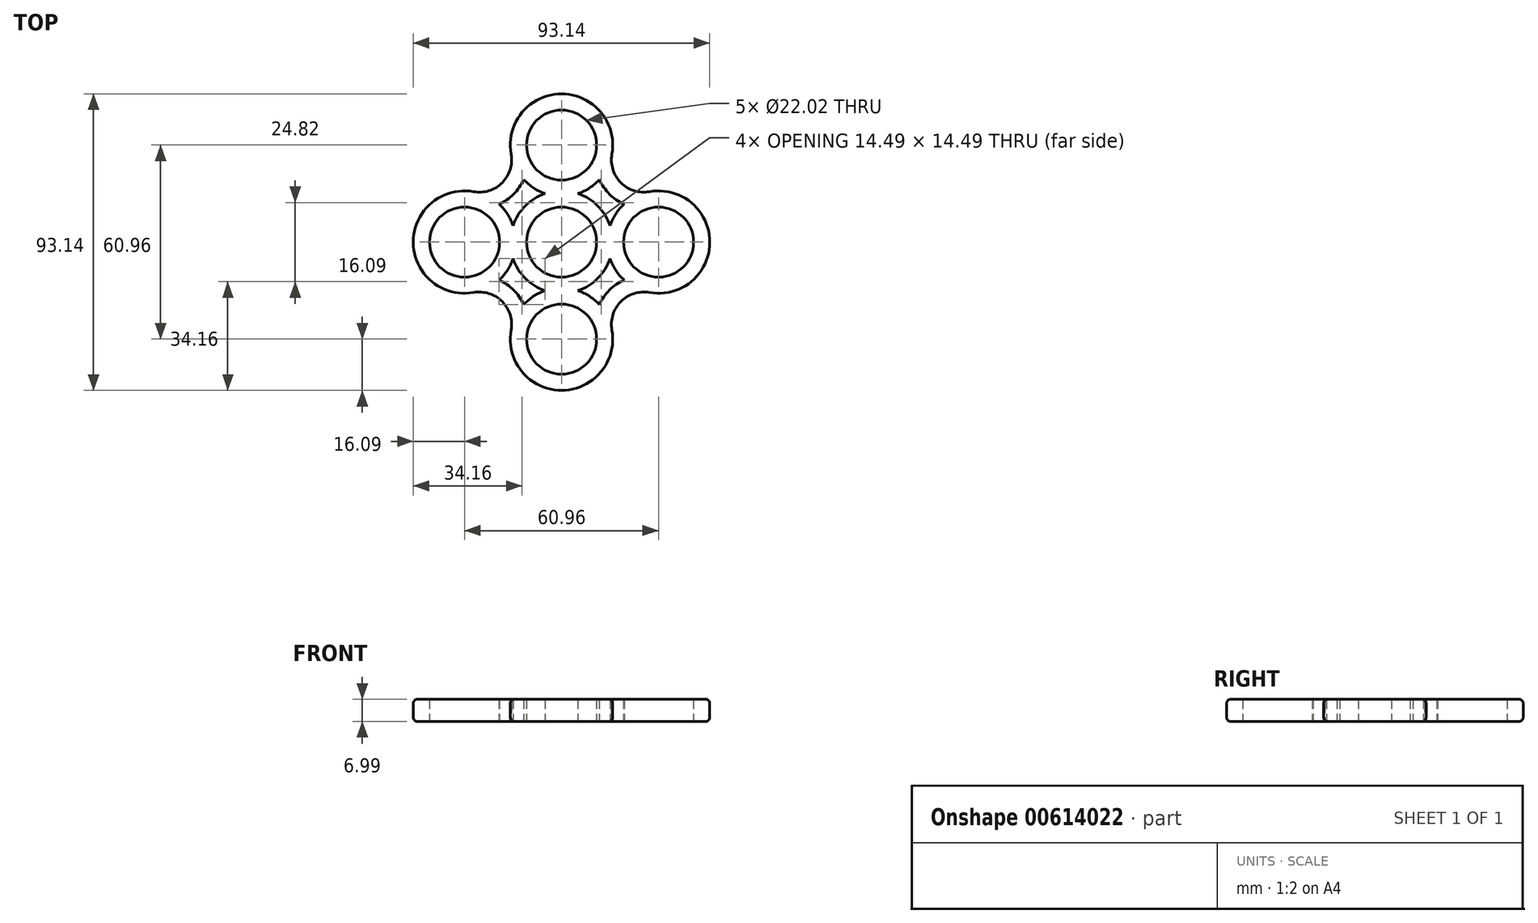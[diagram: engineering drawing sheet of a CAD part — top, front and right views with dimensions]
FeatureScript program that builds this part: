
annotation { "Feature Type Name" : "Feature", "Feature Type Description" : "" }
export const myFeature = defineFeature(function(context is Context, id is Id, definition is map)
    precondition{}
    {
        {
            var Q0;
            Q0=qCreatedBy(makeId("Top.planeOp"),FACE);
            var sketch = newSketch(context, id + "F0", { "sketchPlane" : qUnion([Q0])});
            skCircle(sketch, "E0", {"center": v(0, 0) * mm, "radius": 11.01 * mm});
            skLineSegment(sketch, "E1", {"start": v(0, 0) * mm, "end": v(0, 30.48) * mm});
            skLineSegment(sketch, "E2", {"start": v(0, 0) * mm, "end": v(-30.48, 0) * mm});
            skLineSegment(sketch, "E3", {"start": v(0, 0) * mm, "end": v(30.48, 0) * mm});
            skLineSegment(sketch, "E4", {"start": v(0, 0) * mm, "end": v(0, -30.48) * mm});
            skCircle(sketch, "E5", {"center": v(-30.48, 0) * mm, "radius": 11.01 * mm});
            skCircle(sketch, "E6", {"center": v(0, 30.48) * mm, "radius": 11.01 * mm});
            skCircle(sketch, "E7", {"center": v(30.48, 0) * mm, "radius": 11.01 * mm});
            skCircle(sketch, "E8", {"center": v(-30.48, 0) * mm, "radius": 16.1 * mm});
            skCircle(sketch, "E9", {"center": v(0, 0) * mm, "radius": 17.78 * mm});
            skCircle(sketch, "E10", {"center": v(0, -30.48) * mm, "radius": 16.1 * mm});
            skCircle(sketch, "E11", {"center": v(30.48, 0) * mm, "radius": 16.1 * mm});
            skCircle(sketch, "E12", {"center": v(0, 30.48) * mm, "radius": 16.1 * mm});
            skCircle(sketch, "E13", {"center": v(0, -30.48) * mm, "radius": 11.01 * mm});
            skArc(sketch, "E14", {"start": v(27.63, -15.84) * mm, "mid": v(18.65, -18.65) * mm, "end": v(15.84, -27.63) * mm});
            skArc(sketch, "E15", {"start": v(-15.84, -27.63) * mm, "mid": v(-18.65, -18.65) * mm, "end": v(-27.63, -15.84) * mm});
            skArc(sketch, "E16", {"start": v(15.84, 27.63) * mm, "mid": v(18.65, 18.65) * mm, "end": v(27.63, 15.84) * mm});
            skArc(sketch, "E17", {"start": v(-27.63, 15.84) * mm, "mid": v(-18.65, 18.65) * mm, "end": v(-15.84, 27.63) * mm});
            skSolve(sketch);
        }
        {
            var Q0;
            {var subQ0=sQuery(id+"F0.wireOp",EDGE,"E9");var subQ1=sQuery(id+"F0.wireOp",EDGE,"E1");var subQ2=makeQuery(id+"F0.imprint","INTERSECT",VERTEX,{"derivedFrom":[subQ1,subQ0]});Q0=makeQuery(id+"F0.imprint","IMPRINT",FACE,{"disambiguationData":[TD([[makeQuery(id+"F0.imprint","IMPRINT",EDGE,{"disambiguationData":[TD([[subQ2,1.0]])],"derivedFrom":subQ1}),-1.0]])]});}
            var Q1;
            {var subQ0=sQuery(id+"F0.wireOp",EDGE,"E9");var subQ1=sQuery(id+"F0.wireOp",EDGE,"E1");var subQ2=makeQuery(id+"F0.imprint","INTERSECT",VERTEX,{"derivedFrom":[subQ1,subQ0]});Q1=makeQuery(id+"F0.imprint","IMPRINT",FACE,{"disambiguationData":[TD([[makeQuery(id+"F0.imprint","IMPRINT",EDGE,{"disambiguationData":[TD([[subQ2,1.0]])],"derivedFrom":subQ1}),1.0]])]});}
            var Q2;
            {var subQ0=sQuery(id+"F0.wireOp",EDGE,"E9");var subQ1=sQuery(id+"F0.wireOp",EDGE,"E2");var subQ2=makeQuery(id+"F0.imprint","INTERSECT",VERTEX,{"derivedFrom":[subQ1,subQ0]});Q2=makeQuery(id+"F0.imprint","IMPRINT",FACE,{"disambiguationData":[TD([[makeQuery(id+"F0.imprint","IMPRINT",EDGE,{"disambiguationData":[TD([[subQ2,1.0]])],"derivedFrom":subQ1}),1.0]])]});}
            var Q3;
            {var subQ0=sQuery(id+"F0.wireOp",EDGE,"E9");var subQ1=sQuery(id+"F0.wireOp",EDGE,"E2");var subQ2=makeQuery(id+"F0.imprint","INTERSECT",VERTEX,{"derivedFrom":[subQ1,subQ0]});Q3=makeQuery(id+"F0.imprint","IMPRINT",FACE,{"disambiguationData":[TD([[makeQuery(id+"F0.imprint","IMPRINT",EDGE,{"disambiguationData":[TD([[subQ2,1.0]])],"derivedFrom":subQ1}),-1.0]])]});}
            var Q4;
            {var subQ0=sQuery(id+"F0.wireOp",EDGE,"E9");var subQ1=sQuery(id+"F0.wireOp",EDGE,"E4");var subQ2=makeQuery(id+"F0.imprint","INTERSECT",VERTEX,{"derivedFrom":[subQ1,subQ0]});Q4=makeQuery(id+"F0.imprint","IMPRINT",FACE,{"disambiguationData":[TD([[makeQuery(id+"F0.imprint","IMPRINT",EDGE,{"disambiguationData":[TD([[subQ2,1.0]])],"derivedFrom":subQ1}),-1.0]])]});}
            var Q5;
            {var subQ0=sQuery(id+"F0.wireOp",EDGE,"E9");var subQ1=sQuery(id+"F0.wireOp",EDGE,"E4");var subQ2=makeQuery(id+"F0.imprint","INTERSECT",VERTEX,{"derivedFrom":[subQ1,subQ0]});Q5=makeQuery(id+"F0.imprint","IMPRINT",FACE,{"disambiguationData":[TD([[makeQuery(id+"F0.imprint","IMPRINT",EDGE,{"disambiguationData":[TD([[subQ2,1.0]])],"derivedFrom":subQ1}),1.0]])]});}
            var Q6;
            Q6=makeQuery(id+"F0.imprint","IMPRINT",FACE,{"disambiguationData":[TD([[makeQuery(id+"F0.imprint","IMPRINT",EDGE,{"derivedFrom":sQuery(id+"F0.wireOp",EDGE,"E5")}),-1.0]])]});
            var Q7;
            Q7=makeQuery(id+"F0.imprint","IMPRINT",FACE,{"disambiguationData":[TD([[makeQuery(id+"F0.imprint","IMPRINT",EDGE,{"derivedFrom":sQuery(id+"F0.wireOp",EDGE,"E7")}),-1.0]])]});
            var Q8;
            Q8=makeQuery(id+"F0.imprint","IMPRINT",FACE,{"disambiguationData":[TD([[makeQuery(id+"F0.imprint","IMPRINT",EDGE,{"derivedFrom":sQuery(id+"F0.wireOp",EDGE,"uWeuM5p5-E2Mo-1RXj-Xz4d-7wNfnfuwAmPG")}),-1.0]])]});
            var Q9;
            {var subQ5=sQuery(id+"F0.wireOp",EDGE,"E4");var subQ6=sQuery(id+"F0.wireOp",EDGE,"E0");var subQ7=makeQuery(id+"F0.imprint","INTERSECT",VERTEX,{"derivedFrom":[subQ6,subQ5]});Q9=makeQuery(id+"F0.imprint","IMPRINT",FACE,{"disambiguationData":[TD([[makeQuery(id+"F0.imprint","IMPRINT",EDGE,{"disambiguationData":[TD([[subQ7,-1.0]])],"derivedFrom":subQ6}),-1.0]])]});}
            var Q10;
            {var subQ0=sQuery(id+"F0.wireOp",EDGE,"E11");var subQ1=sQuery(id+"F0.wireOp",EDGE,"E0");var subQ2=makeQuery(id+"F0.imprint","INTERSECT",VERTEX,{"disambiguationData":[OD(0.0)],"derivedFrom":[subQ1,subQ0]});Q10=makeQuery(id+"F0.imprint","IMPRINT",FACE,{"disambiguationData":[TD([[makeQuery(id+"F0.imprint","IMPRINT",EDGE,{"disambiguationData":[TD([[subQ2,-1.0]])],"derivedFrom":subQ1}),-1.0]])]});}
            var Q11;
            {var subQ0=sQuery(id+"F0.wireOp",EDGE,"E3");var subQ1=sQuery(id+"F0.wireOp",EDGE,"E0");var subQ2=makeQuery(id+"F0.imprint","INTERSECT",VERTEX,{"derivedFrom":[subQ1,subQ0]});Q11=makeQuery(id+"F0.imprint","IMPRINT",FACE,{"disambiguationData":[TD([[makeQuery(id+"F0.imprint","IMPRINT",EDGE,{"disambiguationData":[TD([[subQ2,-1.0]])],"derivedFrom":subQ1}),-1.0]])]});}
            var Q12;
            {var subQ0=sQuery(id+"F0.wireOp",EDGE,"E1");var subQ1=sQuery(id+"F0.wireOp",EDGE,"E0");var subQ2=makeQuery(id+"F0.imprint","INTERSECT",VERTEX,{"derivedFrom":[subQ1,subQ0]});Q12=makeQuery(id+"F0.imprint","IMPRINT",FACE,{"disambiguationData":[TD([[makeQuery(id+"F0.imprint","IMPRINT",EDGE,{"disambiguationData":[TD([[subQ2,1.0]])],"derivedFrom":subQ1}),-1.0]])]});}
            var Q13;
            {var subQ3=sQuery(id+"F0.wireOp",EDGE,"E2");var subQ9=sQuery(id+"F0.wireOp",EDGE,"E0");var subQ11=makeQuery(id+"F0.imprint","INTERSECT",VERTEX,{"derivedFrom":[subQ9,subQ3]});Q13=makeQuery(id+"F0.imprint","IMPRINT",FACE,{"disambiguationData":[TD([[makeQuery(id+"F0.imprint","IMPRINT",EDGE,{"disambiguationData":[TD([[subQ11,1.0]])],"derivedFrom":subQ9}),-1.0]])]});}
            var Q14;
            {var subQ3=sQuery(id+"F0.wireOp",EDGE,"E2");var subQ5=sQuery(id+"F0.wireOp",EDGE,"E0");var subQ6=makeQuery(id+"F0.imprint","INTERSECT",VERTEX,{"derivedFrom":[subQ5,subQ3]});Q14=makeQuery(id+"F0.imprint","IMPRINT",FACE,{"disambiguationData":[TD([[makeQuery(id+"F0.imprint","IMPRINT",EDGE,{"disambiguationData":[TD([[subQ6,-1.0]])],"derivedFrom":subQ5}),-1.0]])]});}
            var Q15;
            Q15=makeQuery(id+"F0.imprint","IMPRINT",FACE,{"disambiguationData":[TD([[makeQuery(id+"F0.imprint","IMPRINT",EDGE,{"derivedFrom":sQuery(id+"F0.wireOp",EDGE,"E6")}),-1.0]])]});
            var Q16;
            {var subQ0=sQuery(id+"F0.wireOp",EDGE,"E9");var subQ1=sQuery(id+"F0.wireOp",EDGE,"E3");var subQ2=makeQuery(id+"F0.imprint","INTERSECT",VERTEX,{"derivedFrom":[subQ1,subQ0]});Q16=makeQuery(id+"F0.imprint","IMPRINT",FACE,{"disambiguationData":[TD([[makeQuery(id+"F0.imprint","IMPRINT",EDGE,{"disambiguationData":[TD([[subQ2,1.0]])],"derivedFrom":subQ1}),1.0]])]});}
            var Q17;
            {var subQ0=sQuery(id+"F0.wireOp",EDGE,"E9");var subQ1=sQuery(id+"F0.wireOp",EDGE,"E3");var subQ2=makeQuery(id+"F0.imprint","INTERSECT",VERTEX,{"derivedFrom":[subQ1,subQ0]});Q17=makeQuery(id+"F0.imprint","IMPRINT",FACE,{"disambiguationData":[TD([[makeQuery(id+"F0.imprint","IMPRINT",EDGE,{"disambiguationData":[TD([[subQ2,1.0]])],"derivedFrom":subQ1}),-1.0]])]});}
            var Q18;
            Q18=makeQuery(id+"F0.imprint","IMPRINT",FACE,{"disambiguationData":[TD([[makeQuery(id+"F0.imprint","IMPRINT",EDGE,{"derivedFrom":sQuery(id+"F0.wireOp",EDGE,"E13")}),-1.0]])]});
            var Q19;
            {var subQ0=sQuery(id+"F0.wireOp",EDGE,"E17");Q19=makeQuery(id+"F0.imprint","IMPRINT",FACE,{"disambiguationData":[TD([[makeQuery(id+"F0.imprint","IMPRINT",EDGE,{"derivedFrom":subQ0}),-1.0]])]});}
            var Q20;
            {var subQ5=sQuery(id+"F0.wireOp",EDGE,"E16");Q20=makeQuery(id+"F0.imprint","IMPRINT",FACE,{"disambiguationData":[TD([[makeQuery(id+"F0.imprint","IMPRINT",EDGE,{"derivedFrom":subQ5}),-1.0]])]});}
            var Q21;
            {var subQ5=sQuery(id+"F0.wireOp",EDGE,"E14");Q21=makeQuery(id+"F0.imprint","IMPRINT",FACE,{"disambiguationData":[TD([[makeQuery(id+"F0.imprint","IMPRINT",EDGE,{"derivedFrom":subQ5}),-1.0]])]});}
            var Q22;
            {var subQ0=sQuery(id+"F0.wireOp",EDGE,"E15");Q22=makeQuery(id+"F0.imprint","IMPRINT",FACE,{"disambiguationData":[TD([[makeQuery(id+"F0.imprint","IMPRINT",EDGE,{"derivedFrom":subQ0}),-1.0]])]});}
            extrude(context, id + "F1", {"entities" : qUnion([Q0, Q1, Q2, Q3, Q4, Q5, Q6, Q7, Q8, Q9, Q10, Q11, Q12, Q13, Q14, Q15, Q16, Q17, Q18, Q19, Q20, Q21, Q22]), "depth" : 7 * mm, "offsetDistance" : 25.4 * mm});
        }
        {
            var Q0;
            Q0=makeQuery(id+"F1.opExtrude","CAP_FACE",FACE,{"disambiguationData":[OSD([sQuery(id+"F0.wireOp",EDGE,"E0"),sQuery(id+"F0.wireOp",EDGE,"E5"),sQuery(id+"F0.wireOp",EDGE,"E6"),sQuery(id+"F0.wireOp",EDGE,"E7"),sQuery(id+"F0.wireOp",EDGE,"E8"),sQuery(id+"F0.wireOp",EDGE,"E10"),sQuery(id+"F0.wireOp",EDGE,"E11"),sQuery(id+"F0.wireOp",EDGE,"E12"),sQuery(id+"F0.wireOp",EDGE,"E13"),sQuery(id+"F0.wireOp",EDGE,"E14"),sQuery(id+"F0.wireOp",EDGE,"E15"),sQuery(id+"F0.wireOp",EDGE,"E16"),sQuery(id+"F0.wireOp",EDGE,"E17")])],"isStart":false});
            var Q1;
            Q1=makeQuery(id+"F1.opExtrude","CAP_FACE",FACE,{"disambiguationData":[OSD([sQuery(id+"F0.wireOp",EDGE,"E0"),sQuery(id+"F0.wireOp",EDGE,"E5"),sQuery(id+"F0.wireOp",EDGE,"E6"),sQuery(id+"F0.wireOp",EDGE,"E7"),sQuery(id+"F0.wireOp",EDGE,"E8"),sQuery(id+"F0.wireOp",EDGE,"E10"),sQuery(id+"F0.wireOp",EDGE,"E11"),sQuery(id+"F0.wireOp",EDGE,"E12"),sQuery(id+"F0.wireOp",EDGE,"E13"),sQuery(id+"F0.wireOp",EDGE,"E14"),sQuery(id+"F0.wireOp",EDGE,"E15"),sQuery(id+"F0.wireOp",EDGE,"E16"),sQuery(id+"F0.wireOp",EDGE,"E17")])],"isStart":true});
            shell(context, id + "F2", {"entities" : qUnion([Q0, Q1]), "thickness" : 5.08 * mm});
        }
        {
            var Q0;
            Q0=makeQuery(id+"F1.opExtrude","CAP_EDGE",EDGE,{"disambiguationData":[OSD([sQuery(id+"F0.wireOp",EDGE,"E8")])],"isStart":false});
            fillet(context, id + "F3", {"entities" : qUnion([Q0]), "radius" : 1.27 * mm, "tangentPropagation" : true, "allowEdgeOverflow" : false});
        }
        {
            var Q0;
            Q0=makeQuery(id+"F1.opExtrude","CAP_EDGE",EDGE,{"disambiguationData":[OSD([sQuery(id+"F0.wireOp",EDGE,"E8")])],"isStart":true});
            fillet(context, id + "F4", {"entities" : qUnion([Q0]), "radius" : 1.27 * mm, "tangentPropagation" : true, "allowEdgeOverflow" : false});
        }
    });
